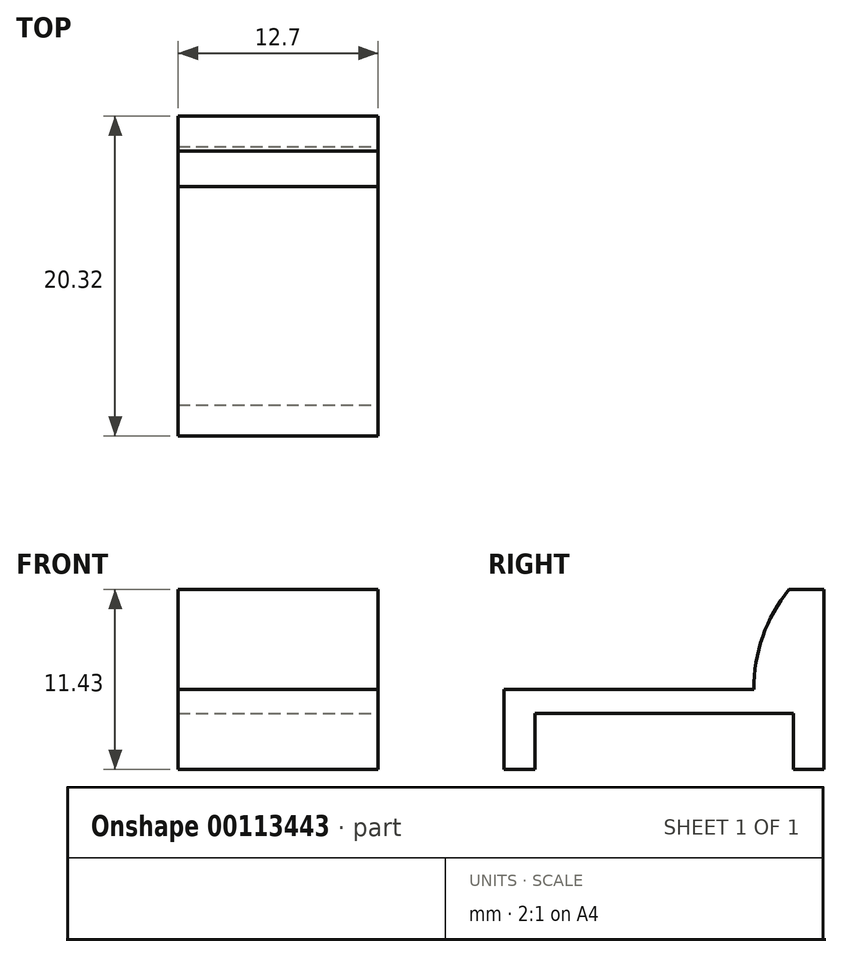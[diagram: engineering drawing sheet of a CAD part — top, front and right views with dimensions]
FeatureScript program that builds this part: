
annotation { "Feature Type Name" : "Feature", "Feature Type Description" : "" }
export const myFeature = defineFeature(function(context is Context, id is Id, definition is map)
    precondition{}
    {
        {
            var Q0;
            Q0=qCreatedBy(makeId("Top.planeOp"),FACE);
            var sketch = newSketch(context, id + "F0", { "sketchPlane" : qUnion([Q0])});
            skLineSegment(sketch, "E0.bottom", {"start": v(6.35, 12.68) * mm, "end": v(-6.35, 12.68) * mm});
            skLineSegment(sketch, "E0.top", {"start": v(6.35, -7.64) * mm, "end": v(-6.35, -7.64) * mm});
            skLineSegment(sketch, "E0.left", {"start": v(6.35, 12.68) * mm, "end": v(6.35, -7.64) * mm});
            skLineSegment(sketch, "E0.right", {"start": v(-6.35, 12.68) * mm, "end": v(-6.35, -7.64) * mm});
            skPoint(sketch, "E0.middle", {"position": v(0, 2.52) * mm});
            skSolve(sketch);
        }
        {
            var Q0;
            Q0=makeQuery(id+"F0.imprint","IMPRINT",FACE,{"disambiguationData":[TD([[makeQuery(id+"F0.imprint","IMPRINT",EDGE,{"derivedFrom":sQuery(id+"F0.wireOp",EDGE,"E0.bottom")}),1.0]])]});
            extrude(context, id + "F1", {"entities" : qUnion([Q0]), "depth" : 5.08 * mm});
        }
        {
            var Q0;
            Q0=makeQuery(id+"F1.opExtrude","CAP_FACE",FACE,{"disambiguationData":[OSD([sQuery(id+"F0.wireOp",EDGE,"E0.bottom"),sQuery(id+"F0.wireOp",EDGE,"E0.top"),sQuery(id+"F0.wireOp",EDGE,"E0.left"),sQuery(id+"F0.wireOp",EDGE,"E0.right")])],"isStart":false});
            var sketch = newSketch(context, id + "F2", { "sketchPlane" : qUnion([Q0])});
            skLineSegment(sketch, "E1.bottom", {"start": v(-6.35, 12.68) * mm, "end": v(6.35, 12.68) * mm});
            skLineSegment(sketch, "E1.top", {"start": v(-6.35, 8.21) * mm, "end": v(6.35, 8.21) * mm});
            skLineSegment(sketch, "E1.left", {"start": v(-6.35, 12.68) * mm, "end": v(-6.35, 8.21) * mm});
            skLineSegment(sketch, "E1.right", {"start": v(6.35, 12.68) * mm, "end": v(6.35, 8.21) * mm});
            skSolve(sketch);
        }
        {
            var Q0;
            Q0=makeQuery(id+"F2.imprint","IMPRINT",FACE,{"disambiguationData":[TD([[makeQuery(id+"F2.imprint","IMPRINT",EDGE,{"derivedFrom":sQuery(id+"F2.wireOp",EDGE,"E1.bottom")}),1.0]])]});
            extrude(context, id + "F3", {"entities" : qUnion([Q0]), "operationType" : NewBodyOperationType.ADD, "depth" : 6.35 * mm});
        }
        {
            var Q0;
            Q0=makeQuery(id+"F3.boolean.opBoolean","MERGE",FACE,{"derivedFrom":[makeQuery(id+"F1.opExtrude","SWEPT_FACE",FACE,{"disambiguationData":[OSD([sQuery(id+"F0.wireOp",EDGE,"E0.left")])]}),makeQuery(id+"F3.opExtrude","SWEPT_FACE",FACE,{"disambiguationData":[OSD([sQuery(id+"F2.wireOp",EDGE,"E1.right")])]})]});
            var sketch = newSketch(context, id + "F4", { "sketchPlane" : qUnion([Q0])});
            skArc(sketch, "E2", {"start": v(10.45, 11.43) * mm, "mid": v(8.79, 8.45) * mm, "end": v(8.21, 5.08) * mm});
            skSolve(sketch);
        }
        {
            var Q0;
            {var subQ0=sQuery(id+"F4.wireOp",EDGE,"E2");Q0=makeQuery(id+"F4.imprint","IMPRINT",FACE,{"disambiguationData":[TD([[makeQuery(id+"F4.imprint","IMPRINT",EDGE,{"derivedFrom":subQ0}),-1.0]])]});}
            extrude(context, id + "F5", {"entities" : qUnion([Q0]), "operationType" : NewBodyOperationType.REMOVE, "oppositeDirection" : true, "depth" : 25.4 * mm});
        }
        {
            var Q0;
            Q0=makeQuery(id+"F3.boolean.opBoolean","MERGE",FACE,{"derivedFrom":[makeQuery(id+"F1.opExtrude","SWEPT_FACE",FACE,{"disambiguationData":[OSD([sQuery(id+"F0.wireOp",EDGE,"E0.left")])]}),makeQuery(id+"F3.opExtrude","SWEPT_FACE",FACE,{"disambiguationData":[OSD([sQuery(id+"F2.wireOp",EDGE,"E1.right")])]})]});
            var sketch = newSketch(context, id + "F6", { "sketchPlane" : qUnion([Q0])});
            skLineSegment(sketch, "E3.bottom", {"start": v(-5.68, 0) * mm, "end": v(10.73, 0) * mm});
            skLineSegment(sketch, "E3.top", {"start": v(-5.68, 3.56) * mm, "end": v(10.73, 3.56) * mm});
            skLineSegment(sketch, "E3.left", {"start": v(-5.68, 0) * mm, "end": v(-5.68, 3.56) * mm});
            skLineSegment(sketch, "E3.right", {"start": v(10.73, 0) * mm, "end": v(10.73, 3.56) * mm});
            skSolve(sketch);
        }
        {
            var Q0;
            Q0=makeQuery(id+"F6.imprint","IMPRINT",FACE,{"disambiguationData":[TD([[makeQuery(id+"F6.imprint","IMPRINT",EDGE,{"derivedFrom":sQuery(id+"F6.wireOp",EDGE,"E3.bottom")}),-1.0]])]});
            extrude(context, id + "F7", {"entities" : qUnion([Q0]), "operationType" : NewBodyOperationType.REMOVE, "oppositeDirection" : true, "depth" : 25.4 * mm});
        }
    });
